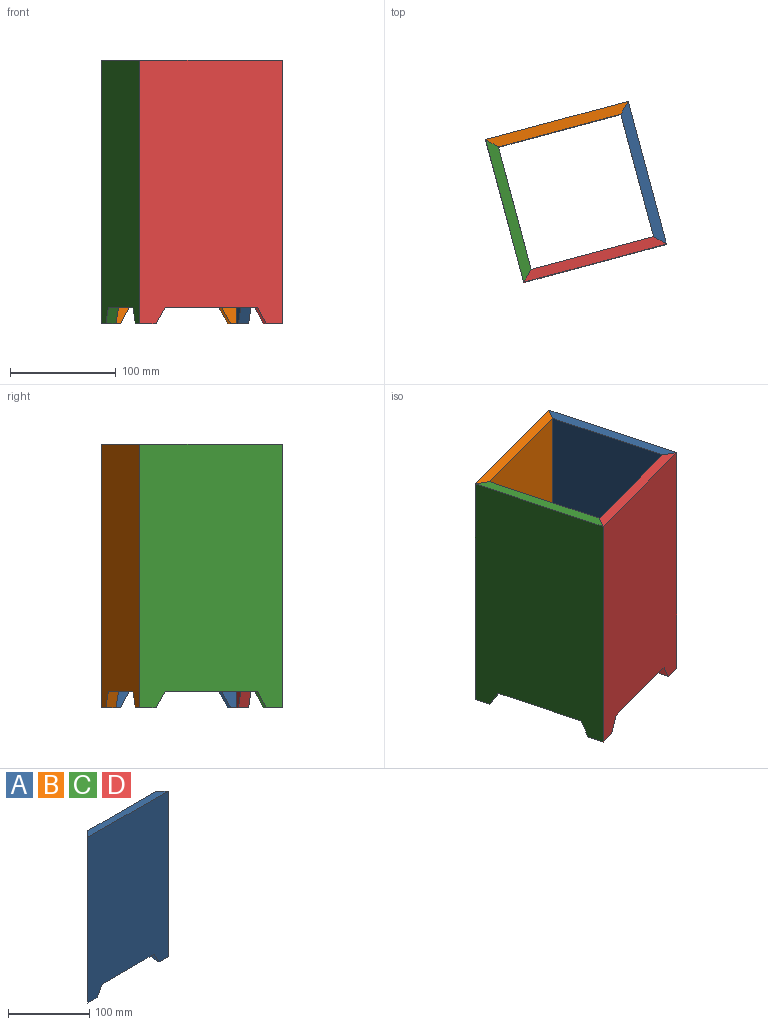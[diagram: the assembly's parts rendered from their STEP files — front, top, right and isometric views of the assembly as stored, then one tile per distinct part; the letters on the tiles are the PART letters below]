
ASSEMBLY  parts=4 mates=3
PART A: 10 faces, bbox 140x10x250 mm
  f0: plane 140x10mm, normal (0,0,1), area 1300mm2, adj f6,f7,f8,f9
  f1: plane 16x10mm, normal (0,0,-1), area 110mm2, adj f2,f6,f7,f9
  f2: plane 16x10mm, normal (0.87,0,-0.49), area 183.6mm2, adj f1,f3,f6,f7
  f3: plane 90.5x10mm, normal (0,0,-1), area 905mm2, adj f2,f4,f6,f7
  f4: plane 16x10mm, normal (-0.88,0,-0.47), area 181.2mm2, adj f3,f5,f6,f7
  f5: plane 16x10mm, normal (0,0,-1), area 110mm2, adj f4,f6,f7,f8
  f6: plane 250x140mm, normal (0,-1,0), area 33412mm2, adj f0,f1,f2,f3,f4,f5,f8,f9
  f7: plane 250x120mm, normal (0,1,0), area 28412mm2, adj f0,f1,f2,f3,f4,f5,f8,f9
  f8: plane 250x10mm, normal (0.71,0.71,0), area 3535.5mm2, adj f0,f5,f6,f7
  f9: plane 250x10mm, normal (-0.71,0.71,0), area 3535.5mm2, adj f0,f1,f6,f7
PART B: same geometry as A
PART C: same geometry as A
PART D: same geometry as A
PLACE A rot(axis=(0,0,1),105deg) t=(60.37,21.93,-8.12)mm
PLACE B rot(axis=(0,0,-1),165deg) t=(-13.12,64.36,-8.12)mm
PLACE C rot(axis=(0,0,-1),75deg) t=(-55.54,-9.12,-8.12)mm
PLACE D rot(axis=(0,0,1),15deg) t=(17.94,-51.55,-8.12)mm
MATE parallel A.f8 <-> A.f8  axis (-0.87,0.5,0) through (48.38,86.01,-8.12)mm
MATE parallel A.f9 <-> A.f9  axis (-0.5,-0.87,0) through (82.02,-39.56,-8.12)mm
MATE parallel C.f9 <-> B.f8  axis (0.5,0.87,0) through (-77.19,52.37,-8.12)mm
